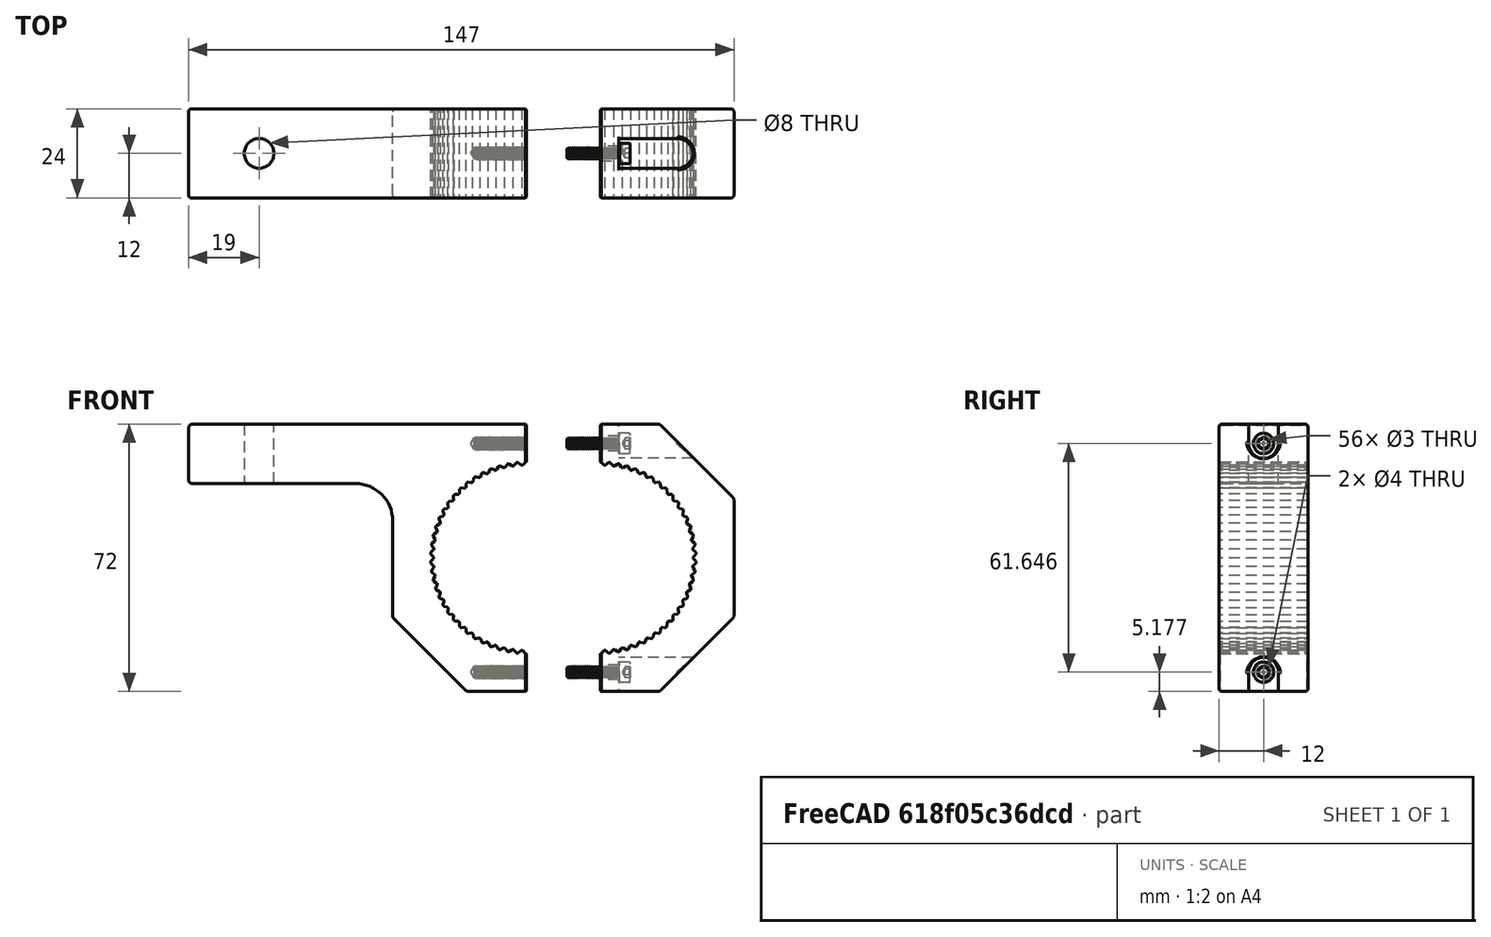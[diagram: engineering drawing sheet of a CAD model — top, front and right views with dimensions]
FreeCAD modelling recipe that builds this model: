
FCSTD DOCUMENT  (FreeCAD 1.0R39319 (Git))
Label: SplitClamp
License: All rights reserved
LicenseURL: https://en.wikipedia.org/wiki/All_rights_reserved
objects: Sketcher::SketchObject×9, PartDesign::Pocket×6, PartDesign::Fillet×5, Part::FeaturePython×5, PartDesign::Chamfer×3, PartDesign::Body×3, PartDesign::Pad×2, PartDesign::FeatureBase×2, Part::Extrusion×1, PartDesign::PolarPattern×1, App::DocumentObjectGroup×1, PartDesign::Hole×1
note: 84 computed .brp shape members not serialized (recipe doc carries the construction recipe); baked Part::Feature solids carry a one-line shape summary decoded from their .brp

FEATURE [Sketcher::SketchObject] Sketch
  ArcFitTolerance = 1e-06
  AttachmentSupport = -> [XZ_Plane]
  FullyConstrained = true
  MakeInternals = false
  MapMode = 5
  Placement = pos=(0,0,0) rot=(1,0,0;1.5708rad)
  sketch-geometry (5):
    g0: LineSegment StartX=-36 StartY=-36 StartZ=0 EndX=36 EndY=-36 EndZ=0
    g1: LineSegment StartX=36 StartY=-36 StartZ=0 EndX=36 EndY=36 EndZ=0
    g2: LineSegment StartX=36 StartY=36 StartZ=0 EndX=-36 EndY=36 EndZ=0
    g3: LineSegment StartX=-36 StartY=36 StartZ=0 EndX=-36 EndY=-36 EndZ=0
    g4: GeomPoint [constr] X=0 Y=0 Z=0
  constraints (12):
    c: Coincident(g0,g1)
    c: Coincident(g1,g2)
    c: Coincident(g2,g3)
    c: Coincident(g3,g0)
    c: Horizontal(g0)
    c: Horizontal(g2)
    c: Vertical(g1)
    c: Vertical(g3)
    c: Symmetric(g2,g0,g4)
    c: Distance(g1,g3) = 72
    c: Distance(g0,g2) = 72
    c: Coincident(g4,g-1)
FEATURE [PartDesign::Pad] Pad
  Direction = (0,-1,2e-16)
  Length = 24
  Length2 = 10
  Midplane = true
  Placement = pos=(0,0,0) rot=(1,0,0;1.5708rad)
  Profile = -> Sketch
  ReferenceAxis = -> Sketch [N_Axis]
  Refine = true
  Suppressed = false
  Type = 0
FEATURE [Sketcher::SketchObject] Sketch001
  ArcFitTolerance = 1e-06
  AttachmentSupport = -> [Pad]
  ExternalGeometry = -> [Pad]
  FullyConstrained = true
  MakeInternals = false
  MapMode = 5
  Placement = pos=(0,-12,0) rot=(1,0,0;1.5708rad)
  sketch-geometry (4):
    g0: LineSegment StartX=0 StartY=20 StartZ=0 EndX=0 EndY=36 EndZ=0
    g1: LineSegment StartX=0 StartY=36 StartZ=0 EndX=-91 EndY=36 EndZ=0
    g2: LineSegment StartX=-91 StartY=36 StartZ=0 EndX=-91 EndY=20 EndZ=0
    g3: LineSegment StartX=-91 StartY=20 StartZ=0 EndX=0 EndY=20 EndZ=0
  constraints (12):
    c: Coincident(g0,g1)
    c: Coincident(g1,g2)
    c: Coincident(g2,g3)
    c: Coincident(g3,g0)
    c: Vertical(g0)
    c: Vertical(g2)
    c: Horizontal(g1)
    c: Horizontal(g3)
    c: Distance(g0,g2) = 91
    c: Distance(g1,g3) = 16
    c: PointOnObject(g0,g-2)
    c: PointOnObject(g0,g-3)
FEATURE [PartDesign::Pad] Pad001
  BaseFeature = -> Pad
  Direction = (0,-1,2e-16)
  Length = 10
  Length2 = 10
  Placement = pos=(0,0,0) rot=(1,0,0;1.5708rad)
  Profile = -> Sketch001
  ReferenceAxis = -> Sketch001 [N_Axis]
  Refine = true
  Suppressed = false
  Type = 3
  UpToFace = -> Pad [Face5]
FEATURE [Sketcher::SketchObject] Sketch002
  ArcFitTolerance = 1e-06
  AttachmentSupport = -> [Pad001]
  FullyConstrained = true
  MakeInternals = false
  MapMode = 5
  Placement = pos=(0,-12,2.8e-15) rot=(1,0,0;1.5708rad)
  sketch-geometry (1):
    g0: Circle CenterX=0 CenterY=0 CenterZ=0 NormalX=0 NormalY=0 NormalZ=1 AngleXU=0 Radius=25
  constraints (2):
    c: Diameter(g0) = 50
    c: Coincident(g0,g-1)
FEATURE [PartDesign::Pocket] Pocket
  BaseFeature = -> Pad001
  Direction = (0,1,-2e-16)
  Length = 5
  Length2 = 5
  Placement = pos=(0,0,0) rot=(1,0,0;1.5708rad)
  Profile = -> Sketch002
  ReferenceAxis = -> Sketch002 [N_Axis]
  Refine = true
  Suppressed = false
  Type = 1
FEATURE [Sketcher::SketchObject] Sketch003
  ArcFitTolerance = 1e-06
  AttachmentSupport = -> [Pocket]
  FullyConstrained = true
  MakeInternals = false
  MapMode = 5
  Placement = pos=(0,-12,2.8e-15) rot=(1,0,0;1.5708rad)
  sketch-geometry (3):
    g0: LineSegment StartX=-1.5 StartY=24.5 StartZ=0 EndX=0 EndY=26 EndZ=0
    g1: LineSegment StartX=0 StartY=26 StartZ=0 EndX=1.5 EndY=24.5 EndZ=0
    g2: LineSegment StartX=1.5 StartY=24.5 StartZ=0 EndX=-1.5 EndY=24.5 EndZ=0
  constraints (9):
    c: Coincident(g0,g1)
    c: Coincident(g1,g2)
    c: Coincident(g2,g0)
    c: Horizontal(g2)
    c: Perpendicular(g0,g1)
    c: DistanceX(g2,g2) = 3
    c: Equal(g1,g0)
    c: PointOnObject(g0,g-2)
    c: DistanceY(g-1,g0) = 26
FEATURE [Sketcher::SketchObject] Sketch004
  ArcFitTolerance = 1e-06
  FullyConstrained = false
  MakeInternals = false
  Placement = pos=(0,22,0) rot=(1,0,0;1.5708rad)
  sketch-geometry (1):
    g0: LineSegment StartX=0 StartY=52.6725 StartZ=0 EndX=0 EndY=-52.0433 EndZ=0
  constraints (2):
    c: PointOnObject(g0,g-2)
    c: PointOnObject(g0,g-2)
FEATURE [Part::Extrusion] Extrude
  Base = -> Sketch004
  Dir = (0,-1,2e-16)
  DirMode = 2
  FaceMakerClass = Part::FaceMakerBullseye
  FaceMakerMode = 3
  LengthFwd = 50
  LengthRev = 0
  Solid = false
  Symmetric = false
FEATURE [PartDesign::Chamfer] Chamfer
  Angle = 45
  Base = -> Pocket [Edge8,Edge2,Edge1]
  BaseFeature = -> Pocket
  ChamferType = 0
  FlipDirection = false
  Placement = pos=(0,0,0) rot=(1,0,0;1.5708rad)
  Refine = true
  Size = 20
  Size2 = 1
  SupportTransform = false
  Suppressed = false
  UseAllEdges = false
FEATURE [PartDesign::Fillet] Fillet
  Base = -> Chamfer [Edge25]
  BaseFeature = -> Chamfer
  Placement = pos=(0,0,0) rot=(1,0,0;1.5708rad)
  Radius = 10
  Refine = true
  SupportTransform = false
  Suppressed = false
  UseAllEdges = false
FEATURE [PartDesign::Fillet] Fillet001
  Base = -> Fillet [Edge17,Edge13,Edge21,Edge25,Edge29,Edge27,Edge20,Edge24]
  BaseFeature = -> Fillet
  Placement = pos=(0,0,0) rot=(1,0,0;1.5708rad)
  Radius = 1
  Refine = true
  SupportTransform = false
  Suppressed = false
  UseAllEdges = false
FEATURE [PartDesign::Fillet] Fillet002
  Base = -> Fillet001 [Edge13,Edge46]
  BaseFeature = -> Fillet001
  Placement = pos=(0,0,0) rot=(1,0,0;1.5708rad)
  Radius = 0.75
  Refine = true
  SupportTransform = false
  Suppressed = false
  UseAllEdges = false
FEATURE [Sketcher::SketchObject] Sketch005
  ArcFitTolerance = 1e-06
  AttachmentSupport = -> [Fillet002]
  FullyConstrained = true
  MakeInternals = false
  MapMode = 5
  Placement = pos=(0,1.58e-14,36) rot=(0,0,1;3.14159rad)
  sketch-geometry (1):
    g0: Circle CenterX=72 CenterY=0 CenterZ=0 NormalX=0 NormalY=0 NormalZ=1 AngleXU=0 Radius=4
  constraints (3):
    c: Diameter(g0) = 8
    c: PointOnObject(g0,g-1)
    c: DistanceX(g-1,g0) = 72
FEATURE [PartDesign::Pocket] Pocket001
  BaseFeature = -> Fillet002
  Direction = (0,0,-1)
  Length = 5
  Length2 = 5
  Placement = pos=(0,0,0) rot=(1,0,0;1.5708rad)
  Profile = -> Sketch005
  ReferenceAxis = -> Sketch005 [N_Axis]
  Refine = true
  Suppressed = false
  Type = 1
FEATURE [PartDesign::Pocket] Pocket002
  BaseFeature = -> Pocket001
  Direction = (0,1,-2e-16)
  Length = 5
  Length2 = 5
  Placement = pos=(0,0,0) rot=(1,0,0;1.5708rad)
  Profile = -> Sketch003
  ReferenceAxis = -> Sketch003 [N_Axis]
  Refine = true
  Suppressed = false
  Type = 1
FEATURE [PartDesign::Fillet] Fillet003
  Base = -> Pocket002 [Edge61,Edge63,Edge60]
  BaseFeature = -> Pocket002
  Placement = pos=(0,0,0) rot=(1,0,0;1.5708rad)
  Radius = 0.5
  Refine = true
  SupportTransform = false
  Suppressed = false
  UseAllEdges = false
FEATURE [PartDesign::PolarPattern] PolarPattern
  Angle = 360
  Axis = -> Sketch003 [N_Axis]
  BaseFeature = -> Fillet003
  Mode = 0
  Occurrences = 66
  Offset = 120
  Originals = -> [Pocket002,Fillet003]
  Placement = pos=(0,0,0) rot=(1,0,0;1.5708rad)
  Refine = true
  Suppressed = false
  TransformMode = 0
FEATURE [Sketcher::SketchObject] Sketch006
  ArcFitTolerance = 1e-06
  AttachmentSupport = -> [YZ_Plane]
  ExternalGeometry = -> [PolarPattern]
  FullyConstrained = true
  MakeInternals = false
  MapMode = 5
  Placement = pos=(0,0,0) rot=(0.57735,0.57735,0.57735;2.0944rad)
  sketch-geometry (3):
    g0: Circle CenterX=0 CenterY=30.8232 CenterZ=0 NormalX=0 NormalY=0 NormalZ=1 AngleXU=0 Radius=1
    g1: LineSegment [constr] StartX=0 StartY=36 StartZ=0 EndX=0 EndY=25.6464 EndZ=0
    g2: Circle CenterX=0 CenterY=-30.8232 CenterZ=0 NormalX=0 NormalY=0 NormalZ=1 AngleXU=0 Radius=1
  constraints (8):
    c: Diameter(g0) = 2
    c: PointOnObject(g0,g-2)
    c: PointOnObject(g1,g-2)
    c: PointOnObject(g1,g-3)
    c: PointOnObject(g1,g-4)
    c: Symmetric(g1,g1,g0)
    c: Equal(g0,g2)
    c: Symmetric(g0,g2,g-1)
FEATURE [PartDesign::Pocket] Pocket003
  BaseFeature = -> PolarPattern
  Direction = (-1,0,0)
  Length = 5
  Length2 = 5
  Placement = pos=(0,0,0) rot=(1,0,0;1.5708rad)
  Profile = -> Sketch006
  ReferenceAxis = -> Sketch006 [N_Axis]
  Refine = true
  Suppressed = false
  Type = 0
FEATURE [PartDesign::Body] Body
  AllowCompound = false
  Group = -> [Sketch,Pad,Sketch001,Pad001,Sketch002,Pocket,Sketch003,Chamfer,Fillet,Fillet001,Fillet002,Sketch005,Pocket001,Pocket002,Fillet003,PolarPattern,Sketch006,Pocket003]
  Origin = -> Origin
  Tip = -> Pocket003
FEATURE [Part::FeaturePython] Slice  # WARN: FeaturePython — macro-defined, semantics opaque (R4)
  Base = -> Body
  Mode = 1
  Tolerance = 0
  Tools = -> [Extrude]
FEATURE [Part::FeaturePython] Slice_child0  label="Slice.0"  # WARN: FeaturePython — macro-defined, semantics opaque (R4)
  Base = -> Slice
  FilterType = 1
  Invert = false
  OverrideMaxVal = 0
  WindowFrom = 80
  WindowTo = 100
  items = 0
FEATURE [Part::FeaturePython] Slice_child1  label="Slice.1"  # WARN: FeaturePython — macro-defined, semantics opaque (R4)
  Base = -> Slice
  FilterType = 1
  Invert = false
  OverrideMaxVal = 0
  WindowFrom = 80
  WindowTo = 100
  items = 1
FEATURE [App::DocumentObjectGroup] GrExplode_Slice  label="Exploded Slice"
  Group = -> [Slice_child0,Slice_child1]
FEATURE [PartDesign::FeatureBase] BaseFeature
  BaseFeature = -> Slice_child0
  Suppressed = false
FEATURE [Sketcher::SketchObject] Sketch007
  ArcFitTolerance = 1e-06
  AttachmentSupport = -> [BaseFeature]
  ExternalGeometry = -> [BaseFeature]
  FullyConstrained = false
  MakeInternals = false
  MapMode = 5
  Placement = pos=(0,0,0) rot=(0.57735,-0.57735,-0.57735;2.0944rad)
  sketch-geometry (2):
    g0: Circle CenterX=0 CenterY=30.8232 CenterZ=0 NormalX=0 NormalY=0 NormalZ=1 AngleXU=0 Radius=2
    g1: Circle CenterX=0 CenterY=-30.8232 CenterZ=0 NormalX=0 NormalY=0 NormalZ=1 AngleXU=0 Radius=2
  constraints (3):
    c: Diameter(g0) = 4
    c: Coincident(g0,g-3)
    c: Diameter(g1) = 4
FEATURE [PartDesign::Pocket] Pocket004
  BaseFeature = -> BaseFeature
  Direction = (1,0,0)
  Length = 5
  Length2 = 5
  Profile = -> Sketch007
  ReferenceAxis = -> Sketch007 [N_Axis]
  Refine = true
  Suppressed = false
  Type = 1
FEATURE [PartDesign::Chamfer] Chamfer001
  Angle = 45
  Base = -> Pocket004 [Edge181,Edge524]
  BaseFeature = -> Pocket004
  ChamferType = 0
  FlipDirection = false
  Refine = true
  Size = 0.25
  Size2 = 1
  SupportTransform = false
  Suppressed = false
  UseAllEdges = false
FEATURE [Sketcher::SketchObject] Sketch008
  ArcFitTolerance = 1e-06
  AttachmentOffset = pos=(0,0,-5) rot=(0,0,1;0rad)
  AttachmentSupport = -> [Chamfer001]
  ExternalGeometry = -> [Chamfer001]
  FullyConstrained = false
  MakeInternals = false
  MapMode = 5
  Placement = pos=(5,0,0) rot=(0.57735,-0.57735,-0.57735;2.0944rad)
  sketch-geometry (8):
    g0: ArcOfCircle CenterX=0 CenterY=30.8232 CenterZ=0 NormalX=0 NormalY=0 NormalZ=1 AngleXU=0 Radius=4 StartAngle=3.14159 EndAngle=6.28319
    g1: ArcOfCircle CenterX=-4.79e-14 CenterY=40.8232 CenterZ=0 NormalX=0 NormalY=0 NormalZ=1 AngleXU=0 Radius=4 StartAngle=-1.19e-13 EndAngle=3.14159
    g2: LineSegment StartX=-4 StartY=30.8232 StartZ=0 EndX=-4 EndY=40.8232 EndZ=0
    g3: LineSegment StartX=4 StartY=30.8232 StartZ=0 EndX=4 EndY=40.8232 EndZ=0
    g4: LineSegment StartX=-4 StartY=-30.8232 StartZ=0 EndX=-4 EndY=-40.8232 EndZ=0
    g5: ArcOfCircle CenterX=0 CenterY=-30.8232 CenterZ=0 NormalX=0 NormalY=0 NormalZ=1 AngleXU=0 Radius=4 StartAngle=-1.51e-14 EndAngle=3.14159
    g6: LineSegment StartX=4 StartY=-30.8232 StartZ=0 EndX=4 EndY=-40.8232 EndZ=0
    g7: ArcOfCircle CenterX=-4.79e-14 CenterY=-40.8232 CenterZ=0 NormalX=0 NormalY=0 NormalZ=1 AngleXU=0 Radius=4 StartAngle=3.14159 EndAngle=6.28319
  constraints (16):
    c: Tangent(g0,g2) = 1.5708
    c: Tangent(g0,g3) = -1.5708
    c: Tangent(g1,g2) = 1.5708
    c: Tangent(g1,g3) = -1.5708
    c: Equal(g0,g1)
    c: Vertical(g3)
    c: Radius(g0) = 4
    c: Coincident(g0,g-3)
    c: DistanceY(g0,g1) = 10
    c: Tangent(g5,g4) = -1.5708
    c: Tangent(g5,g6) = 1.5708
    c: Tangent(g7,g4) = -1.5708
    c: Tangent(g7,g6) = 1.5708
    c: Equal(g5,g7)
    c: Vertical(g6)
    c: Radius(g5) = 4
FEATURE [PartDesign::Pocket] Pocket005
  BaseFeature = -> Chamfer001
  Direction = (1,0,0)
  Length = 5
  Length2 = 5
  Profile = -> Sketch008
  ReferenceAxis = -> Sketch008 [N_Axis]
  Refine = true
  Suppressed = false
  Type = 1
FEATURE [PartDesign::Fillet] Fillet004
  Base = -> Pocket005 [Edge579,Edge591]
  BaseFeature = -> Pocket005
  Radius = 0.5
  Refine = true
  SupportTransform = false
  Suppressed = false
  UseAllEdges = false
FEATURE [PartDesign::Body] Body001  label="Part2"
  AllowCompound = false
  BaseFeature = -> Slice_child0
  Group = -> [BaseFeature,Sketch007,Pocket004,Chamfer001,Sketch008,Pocket005,Fillet004]
  Origin = -> Origin001
  Placement = pos=(20,0,0) rot=(0,0,1;0rad)
  Tip = -> Fillet004
FEATURE [PartDesign::FeatureBase] BaseFeature001
  BaseFeature = -> Slice_child1
  Suppressed = false
FEATURE [PartDesign::Hole] Hole
  BaseFeature = -> BaseFeature001
  CustomThreadClearance = 0.5
  Depth = 14
  DepthType = 0
  Diameter = 3
  DrillForDepth = false
  DrillPoint = 1
  DrillPointAngle = 118
  HoleCutCountersinkAngle = 90
  HoleCutCustomValues = false
  HoleCutDepth = 0
  HoleCutDiameter = 6.1
  HoleCutType = 0
  ModelThread = true
  Profile = -> BaseFeature001 [Edge192,Edge215]
  Refine = true
  Suppressed = false
  Tapered = false
  TaperedAngle = 90
  ThreadClass = 0
  ThreadDepth = 14
  ThreadDepthType = 0
  ThreadDirection = 0
  ThreadFit = 0
  ThreadSize = 9
  ThreadType = 1
  Threaded = true
  UseCustomThreadClearance = true
FEATURE [PartDesign::Chamfer] Chamfer002
  Angle = 45
  Base = -> Hole [Edge185,Edge217]
  BaseFeature = -> Hole
  ChamferType = 0
  FlipDirection = false
  Refine = true
  Size = 0.25
  Size2 = 1
  SupportTransform = false
  Suppressed = false
  UseAllEdges = false
FEATURE [PartDesign::Body] Body002  label="Part1"
  AllowCompound = false
  BaseFeature = -> Slice_child1
  Group = -> [BaseFeature001,Hole,Chamfer002]
  Origin = -> Origin002
  Tip = -> Chamfer002
FEATURE [Part::FeaturePython] Screw  label="M3x14-Screw"  # WARN: FeaturePython — macro-defined, semantics opaque (R4)
  BaseObject = -> Body001 [Fillet004.Edge24]
  Diameter = 4
  Invert = true
  LeftHanded = false
  Length = 10
  LengthCustom = 14
  MatchOuter = false
  OffsetAngle = 0
  Placement = pos=(25,0,30.8232) rot=(0,1,0;1.5708rad)
  Thread = true
  Type = 75
FEATURE [Part::FeaturePython] Screw001  label="M3x14-Screw001"  # WARN: FeaturePython — macro-defined, semantics opaque (R4)
  BaseObject = -> Body001 [Fillet004.Edge655]
  Diameter = 4
  Invert = true
  LeftHanded = false
  Length = 10
  LengthCustom = 14
  MatchOuter = false
  OffsetAngle = 0
  Placement = pos=(25,0,-30.8232) rot=(0,1,0;1.5708rad)
  Thread = true
  Type = 75
